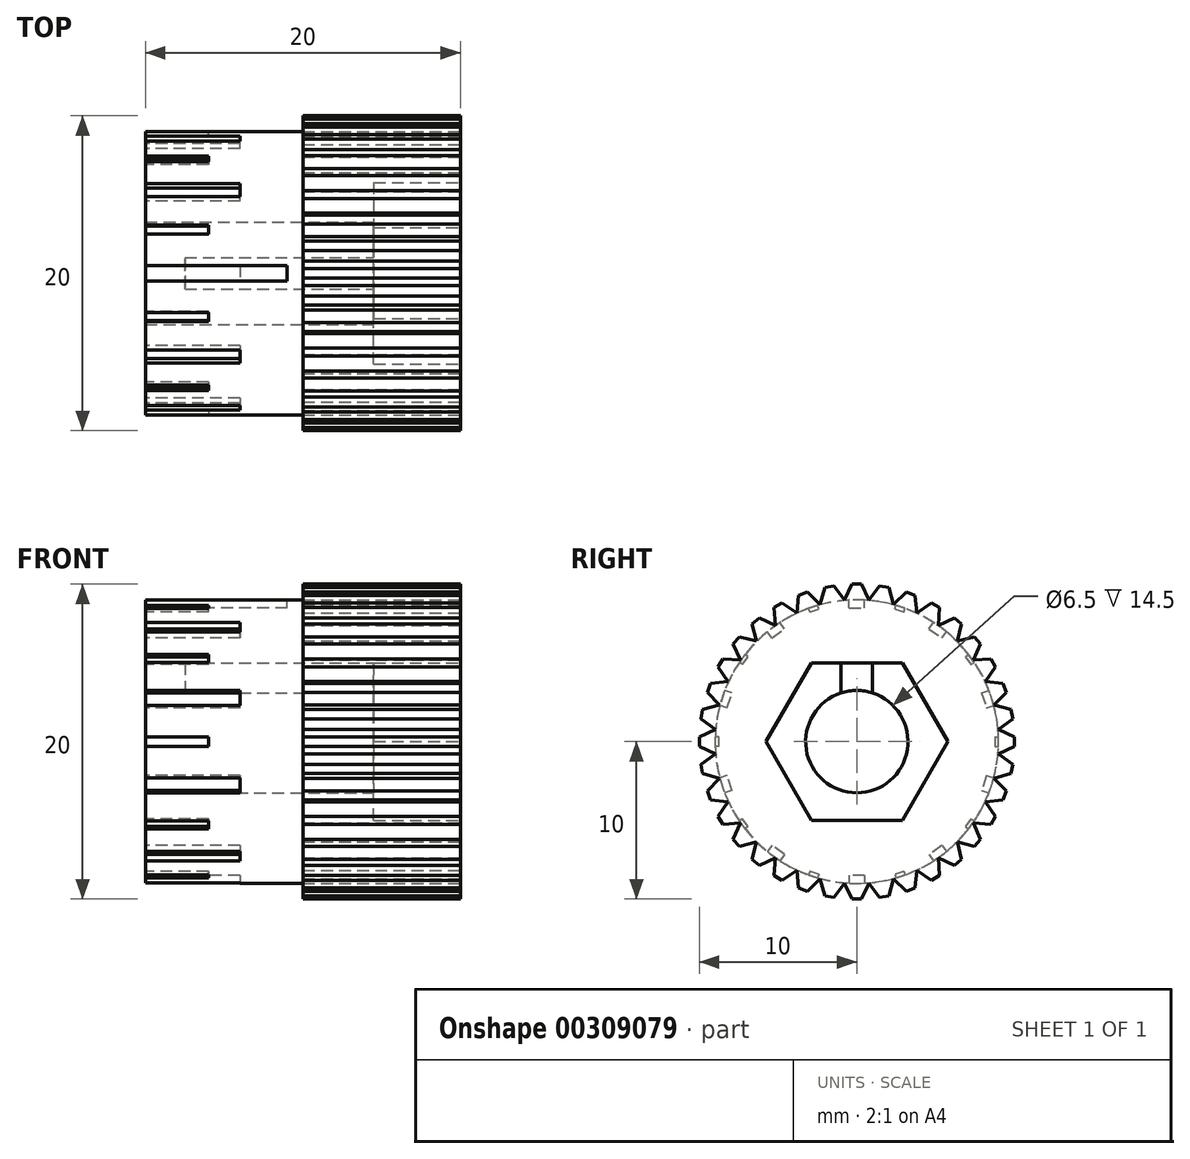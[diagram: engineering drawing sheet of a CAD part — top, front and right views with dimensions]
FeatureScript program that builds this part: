
annotation { "Feature Type Name" : "Feature", "Feature Type Description" : "" }
export const myFeature = defineFeature(function(context is Context, id is Id, definition is map)
    precondition{}
    {
        {
            var Q0;
            Q0=qCreatedBy(makeId("Right.planeOp"),FACE);
            var sketch = newSketch(context, id + "F0", { "sketchPlane" : qUnion([Q0])});
            skCircle(sketch, "E0", {"center": v(0, 0) * mm, "radius": 9 * mm});
            skSolve(sketch);
        }
        {
            var Q0;
            Q0 = qSketchRegion(id + "F0", true);
            extrude(context, id + "F1", {"entities" : qUnion([Q0]), "depth" : 20 * mm});
        }
        {
            var Q0;
            Q0=makeQuery(id+"F1.opExtrude","CAP_FACE",FACE,{"disambiguationData":[OSD([sQuery(id+"F0.wireOp",EDGE,"E0")])],"isStart":false});
            var sketch = newSketch(context, id + "F2", { "sketchPlane" : qUnion([Q0])});
            skLineSegment(sketch, "E1", {"start": v(0, 10) * mm, "end": v(0.3, 10) * mm});
            skLineSegment(sketch, "E2", {"start": v(0.3, 10) * mm, "end": v(0.83, 8.9) * mm});
            skLineSegment(sketch, "E3.MirrorCS", {"start": v(-0.3, 10) * mm, "end": v(-0.83, 8.9) * mm});
            skLineSegment(sketch, "E4.MirrorCS", {"start": v(0, 10) * mm, "end": v(-0.3, 10) * mm});
            skLineSegment(sketch, "E5.1.0", {"start": v(-1.44, 9.9) * mm, "end": v(-0.72, 8.9) * mm});
            skLineSegment(sketch, "E5.1.1", {"start": v(-2.03, 9.8) * mm, "end": v(-2.36, 8.61) * mm});
            skLineSegment(sketch, "E5.1.2", {"start": v(-1.74, 9.85) * mm, "end": v(-1.44, 9.9) * mm});
            skLineSegment(sketch, "E5.1.3", {"start": v(-1.74, 9.85) * mm, "end": v(-2.03, 9.8) * mm});
            skLineSegment(sketch, "E5.2.0", {"start": v(-3.14, 9.5) * mm, "end": v(-2.26, 8.64) * mm});
            skLineSegment(sketch, "E5.2.1", {"start": v(-3.7, 9.3) * mm, "end": v(-3.82, 8.07) * mm});
            skLineSegment(sketch, "E5.2.2", {"start": v(-3.42, 9.4) * mm, "end": v(-3.14, 9.5) * mm});
            skLineSegment(sketch, "E5.2.3", {"start": v(-3.42, 9.4) * mm, "end": v(-3.7, 9.3) * mm});
            skLineSegment(sketch, "E5.3.0", {"start": v(-4.74, 8.81) * mm, "end": v(-3.73, 8.12) * mm});
            skLineSegment(sketch, "E5.3.1", {"start": v(-5.26, 8.51) * mm, "end": v(-5.17, 7.28) * mm});
            skLineSegment(sketch, "E5.3.2", {"start": v(-5, 8.66) * mm, "end": v(-4.74, 8.81) * mm});
            skLineSegment(sketch, "E5.3.3", {"start": v(-5, 8.66) * mm, "end": v(-5.26, 8.51) * mm});
            skLineSegment(sketch, "E5.4.0", {"start": v(-6.2, 7.85) * mm, "end": v(-5.08, 7.35) * mm});
            skLineSegment(sketch, "E5.4.1", {"start": v(-6.66, 7.47) * mm, "end": v(-6.35, 6.28) * mm});
            skLineSegment(sketch, "E5.4.2", {"start": v(-6.43, 7.66) * mm, "end": v(-6.2, 7.85) * mm});
            skLineSegment(sketch, "E5.4.3", {"start": v(-6.43, 7.66) * mm, "end": v(-6.66, 7.47) * mm});
            skLineSegment(sketch, "E5.5.0", {"start": v(-7.47, 6.66) * mm, "end": v(-6.28, 6.35) * mm});
            skLineSegment(sketch, "E5.5.1", {"start": v(-7.85, 6.2) * mm, "end": v(-7.35, 5.08) * mm});
            skLineSegment(sketch, "E5.5.2", {"start": v(-7.66, 6.43) * mm, "end": v(-7.47, 6.66) * mm});
            skLineSegment(sketch, "E5.5.3", {"start": v(-7.66, 6.43) * mm, "end": v(-7.85, 6.2) * mm});
            skLineSegment(sketch, "E5.6.0", {"start": v(-8.51, 5.26) * mm, "end": v(-7.28, 5.17) * mm});
            skLineSegment(sketch, "E5.6.1", {"start": v(-8.81, 4.74) * mm, "end": v(-8.12, 3.73) * mm});
            skLineSegment(sketch, "E5.6.2", {"start": v(-8.66, 5) * mm, "end": v(-8.51, 5.26) * mm});
            skLineSegment(sketch, "E5.6.3", {"start": v(-8.66, 5) * mm, "end": v(-8.81, 4.74) * mm});
            skLineSegment(sketch, "E5.7.0", {"start": v(-9.3, 3.7) * mm, "end": v(-8.07, 3.82) * mm});
            skLineSegment(sketch, "E5.7.1", {"start": v(-9.5, 3.14) * mm, "end": v(-8.64, 2.26) * mm});
            skLineSegment(sketch, "E5.7.2", {"start": v(-9.4, 3.42) * mm, "end": v(-9.3, 3.7) * mm});
            skLineSegment(sketch, "E5.7.3", {"start": v(-9.4, 3.42) * mm, "end": v(-9.5, 3.14) * mm});
            skLineSegment(sketch, "E5.8.0", {"start": v(-9.8, 2.03) * mm, "end": v(-8.61, 2.36) * mm});
            skLineSegment(sketch, "E5.8.1", {"start": v(-9.9, 1.44) * mm, "end": v(-8.9, 0.72) * mm});
            skLineSegment(sketch, "E5.8.2", {"start": v(-9.85, 1.74) * mm, "end": v(-9.8, 2.03) * mm});
            skLineSegment(sketch, "E5.8.3", {"start": v(-9.85, 1.74) * mm, "end": v(-9.9, 1.44) * mm});
            skLineSegment(sketch, "E5.9.0", {"start": v(-10, 0.3) * mm, "end": v(-8.9, 0.83) * mm});
            skLineSegment(sketch, "E5.9.1", {"start": v(-10, -0.3) * mm, "end": v(-8.9, -0.83) * mm});
            skLineSegment(sketch, "E5.9.2", {"start": v(-10, 0) * mm, "end": v(-10, 0.3) * mm});
            skLineSegment(sketch, "E5.9.3", {"start": v(-10, 0) * mm, "end": v(-10, -0.3) * mm});
            skLineSegment(sketch, "E5.10.0", {"start": v(-9.9, -1.44) * mm, "end": v(-8.9, -0.72) * mm});
            skLineSegment(sketch, "E5.10.1", {"start": v(-9.8, -2.03) * mm, "end": v(-8.61, -2.36) * mm});
            skLineSegment(sketch, "E5.10.2", {"start": v(-9.85, -1.74) * mm, "end": v(-9.9, -1.44) * mm});
            skLineSegment(sketch, "E5.10.3", {"start": v(-9.85, -1.74) * mm, "end": v(-9.8, -2.03) * mm});
            skLineSegment(sketch, "E5.11.0", {"start": v(-9.5, -3.14) * mm, "end": v(-8.64, -2.26) * mm});
            skLineSegment(sketch, "E5.11.1", {"start": v(-9.3, -3.7) * mm, "end": v(-8.07, -3.82) * mm});
            skLineSegment(sketch, "E5.11.2", {"start": v(-9.4, -3.42) * mm, "end": v(-9.5, -3.14) * mm});
            skLineSegment(sketch, "E5.11.3", {"start": v(-9.4, -3.42) * mm, "end": v(-9.3, -3.7) * mm});
            skLineSegment(sketch, "E5.12.0", {"start": v(-8.81, -4.74) * mm, "end": v(-8.12, -3.73) * mm});
            skLineSegment(sketch, "E5.12.1", {"start": v(-8.51, -5.26) * mm, "end": v(-7.28, -5.17) * mm});
            skLineSegment(sketch, "E5.12.2", {"start": v(-8.66, -5) * mm, "end": v(-8.81, -4.74) * mm});
            skLineSegment(sketch, "E5.12.3", {"start": v(-8.66, -5) * mm, "end": v(-8.51, -5.26) * mm});
            skLineSegment(sketch, "E5.13.0", {"start": v(-7.85, -6.2) * mm, "end": v(-7.35, -5.08) * mm});
            skLineSegment(sketch, "E5.13.1", {"start": v(-7.47, -6.66) * mm, "end": v(-6.28, -6.35) * mm});
            skLineSegment(sketch, "E5.13.2", {"start": v(-7.66, -6.43) * mm, "end": v(-7.85, -6.2) * mm});
            skLineSegment(sketch, "E5.13.3", {"start": v(-7.66, -6.43) * mm, "end": v(-7.47, -6.66) * mm});
            skLineSegment(sketch, "E5.14.0", {"start": v(-6.66, -7.47) * mm, "end": v(-6.35, -6.28) * mm});
            skLineSegment(sketch, "E5.14.1", {"start": v(-6.2, -7.85) * mm, "end": v(-5.08, -7.35) * mm});
            skLineSegment(sketch, "E5.14.2", {"start": v(-6.43, -7.66) * mm, "end": v(-6.66, -7.47) * mm});
            skLineSegment(sketch, "E5.14.3", {"start": v(-6.43, -7.66) * mm, "end": v(-6.2, -7.85) * mm});
            skLineSegment(sketch, "E5.15.0", {"start": v(-5.26, -8.51) * mm, "end": v(-5.17, -7.28) * mm});
            skLineSegment(sketch, "E5.15.1", {"start": v(-4.74, -8.81) * mm, "end": v(-3.73, -8.12) * mm});
            skLineSegment(sketch, "E5.15.2", {"start": v(-5, -8.66) * mm, "end": v(-5.26, -8.51) * mm});
            skLineSegment(sketch, "E5.15.3", {"start": v(-5, -8.66) * mm, "end": v(-4.74, -8.81) * mm});
            skLineSegment(sketch, "E5.16.0", {"start": v(-3.7, -9.3) * mm, "end": v(-3.82, -8.07) * mm});
            skLineSegment(sketch, "E5.16.1", {"start": v(-3.14, -9.5) * mm, "end": v(-2.26, -8.64) * mm});
            skLineSegment(sketch, "E5.16.2", {"start": v(-3.42, -9.4) * mm, "end": v(-3.7, -9.3) * mm});
            skLineSegment(sketch, "E5.16.3", {"start": v(-3.42, -9.4) * mm, "end": v(-3.14, -9.5) * mm});
            skLineSegment(sketch, "E5.17.0", {"start": v(-2.03, -9.8) * mm, "end": v(-2.36, -8.61) * mm});
            skLineSegment(sketch, "E5.17.1", {"start": v(-1.44, -9.9) * mm, "end": v(-0.72, -8.9) * mm});
            skLineSegment(sketch, "E5.17.2", {"start": v(-1.74, -9.85) * mm, "end": v(-2.03, -9.8) * mm});
            skLineSegment(sketch, "E5.17.3", {"start": v(-1.74, -9.85) * mm, "end": v(-1.44, -9.9) * mm});
            skLineSegment(sketch, "E5.18.0", {"start": v(-0.3, -10) * mm, "end": v(-0.83, -8.9) * mm});
            skLineSegment(sketch, "E5.18.1", {"start": v(0.3, -10) * mm, "end": v(0.83, -8.9) * mm});
            skLineSegment(sketch, "E5.18.2", {"start": v(0, -10) * mm, "end": v(-0.3, -10) * mm});
            skLineSegment(sketch, "E5.18.3", {"start": v(0, -10) * mm, "end": v(0.3, -10) * mm});
            skLineSegment(sketch, "E5.19.0", {"start": v(1.44, -9.9) * mm, "end": v(0.72, -8.9) * mm});
            skLineSegment(sketch, "E5.19.1", {"start": v(2.03, -9.8) * mm, "end": v(2.36, -8.61) * mm});
            skLineSegment(sketch, "E5.19.2", {"start": v(1.74, -9.85) * mm, "end": v(1.44, -9.9) * mm});
            skLineSegment(sketch, "E5.19.3", {"start": v(1.74, -9.85) * mm, "end": v(2.03, -9.8) * mm});
            skLineSegment(sketch, "E5.20.0", {"start": v(3.14, -9.5) * mm, "end": v(2.26, -8.64) * mm});
            skLineSegment(sketch, "E5.20.1", {"start": v(3.7, -9.3) * mm, "end": v(3.82, -8.07) * mm});
            skLineSegment(sketch, "E5.20.2", {"start": v(3.42, -9.4) * mm, "end": v(3.14, -9.5) * mm});
            skLineSegment(sketch, "E5.20.3", {"start": v(3.42, -9.4) * mm, "end": v(3.7, -9.3) * mm});
            skLineSegment(sketch, "E5.21.0", {"start": v(4.74, -8.81) * mm, "end": v(3.73, -8.12) * mm});
            skLineSegment(sketch, "E5.21.1", {"start": v(5.26, -8.51) * mm, "end": v(5.17, -7.28) * mm});
            skLineSegment(sketch, "E5.21.2", {"start": v(5, -8.66) * mm, "end": v(4.74, -8.81) * mm});
            skLineSegment(sketch, "E5.21.3", {"start": v(5, -8.66) * mm, "end": v(5.26, -8.51) * mm});
            skLineSegment(sketch, "E5.22.0", {"start": v(6.2, -7.85) * mm, "end": v(5.08, -7.35) * mm});
            skLineSegment(sketch, "E5.22.1", {"start": v(6.66, -7.47) * mm, "end": v(6.35, -6.28) * mm});
            skLineSegment(sketch, "E5.22.2", {"start": v(6.43, -7.66) * mm, "end": v(6.2, -7.85) * mm});
            skLineSegment(sketch, "E5.22.3", {"start": v(6.43, -7.66) * mm, "end": v(6.66, -7.47) * mm});
            skLineSegment(sketch, "E5.23.0", {"start": v(7.47, -6.66) * mm, "end": v(6.28, -6.35) * mm});
            skLineSegment(sketch, "E5.23.1", {"start": v(7.85, -6.2) * mm, "end": v(7.35, -5.08) * mm});
            skLineSegment(sketch, "E5.23.2", {"start": v(7.66, -6.43) * mm, "end": v(7.47, -6.66) * mm});
            skLineSegment(sketch, "E5.23.3", {"start": v(7.66, -6.43) * mm, "end": v(7.85, -6.2) * mm});
            skLineSegment(sketch, "E5.24.0", {"start": v(8.51, -5.26) * mm, "end": v(7.28, -5.17) * mm});
            skLineSegment(sketch, "E5.24.1", {"start": v(8.81, -4.74) * mm, "end": v(8.12, -3.73) * mm});
            skLineSegment(sketch, "E5.24.2", {"start": v(8.66, -5) * mm, "end": v(8.51, -5.26) * mm});
            skLineSegment(sketch, "E5.24.3", {"start": v(8.66, -5) * mm, "end": v(8.81, -4.74) * mm});
            skLineSegment(sketch, "E5.25.0", {"start": v(9.3, -3.7) * mm, "end": v(8.07, -3.82) * mm});
            skLineSegment(sketch, "E5.25.1", {"start": v(9.5, -3.14) * mm, "end": v(8.64, -2.26) * mm});
            skLineSegment(sketch, "E5.25.2", {"start": v(9.4, -3.42) * mm, "end": v(9.3, -3.7) * mm});
            skLineSegment(sketch, "E5.25.3", {"start": v(9.4, -3.42) * mm, "end": v(9.5, -3.14) * mm});
            skLineSegment(sketch, "E5.26.0", {"start": v(9.8, -2.03) * mm, "end": v(8.61, -2.36) * mm});
            skLineSegment(sketch, "E5.26.1", {"start": v(9.9, -1.44) * mm, "end": v(8.9, -0.72) * mm});
            skLineSegment(sketch, "E5.26.2", {"start": v(9.85, -1.74) * mm, "end": v(9.8, -2.03) * mm});
            skLineSegment(sketch, "E5.26.3", {"start": v(9.85, -1.74) * mm, "end": v(9.9, -1.44) * mm});
            skLineSegment(sketch, "E5.27.0", {"start": v(10, -0.3) * mm, "end": v(8.9, -0.83) * mm});
            skLineSegment(sketch, "E5.27.1", {"start": v(10, 0.3) * mm, "end": v(8.9, 0.83) * mm});
            skLineSegment(sketch, "E5.27.2", {"start": v(10, 0) * mm, "end": v(10, -0.3) * mm});
            skLineSegment(sketch, "E5.27.3", {"start": v(10, 0) * mm, "end": v(10, 0.3) * mm});
            skLineSegment(sketch, "E5.28.0", {"start": v(9.9, 1.44) * mm, "end": v(8.9, 0.72) * mm});
            skLineSegment(sketch, "E5.28.1", {"start": v(9.8, 2.03) * mm, "end": v(8.61, 2.36) * mm});
            skLineSegment(sketch, "E5.28.2", {"start": v(9.85, 1.74) * mm, "end": v(9.9, 1.44) * mm});
            skLineSegment(sketch, "E5.28.3", {"start": v(9.85, 1.74) * mm, "end": v(9.8, 2.03) * mm});
            skLineSegment(sketch, "E5.29.0", {"start": v(9.5, 3.14) * mm, "end": v(8.64, 2.26) * mm});
            skLineSegment(sketch, "E5.29.1", {"start": v(9.3, 3.7) * mm, "end": v(8.07, 3.82) * mm});
            skLineSegment(sketch, "E5.29.2", {"start": v(9.4, 3.42) * mm, "end": v(9.5, 3.14) * mm});
            skLineSegment(sketch, "E5.29.3", {"start": v(9.4, 3.42) * mm, "end": v(9.3, 3.7) * mm});
            skLineSegment(sketch, "E5.30.0", {"start": v(8.81, 4.74) * mm, "end": v(8.12, 3.73) * mm});
            skLineSegment(sketch, "E5.30.1", {"start": v(8.51, 5.26) * mm, "end": v(7.28, 5.17) * mm});
            skLineSegment(sketch, "E5.30.2", {"start": v(8.66, 5) * mm, "end": v(8.81, 4.74) * mm});
            skLineSegment(sketch, "E5.30.3", {"start": v(8.66, 5) * mm, "end": v(8.51, 5.26) * mm});
            skLineSegment(sketch, "E5.31.0", {"start": v(7.85, 6.2) * mm, "end": v(7.35, 5.08) * mm});
            skLineSegment(sketch, "E5.31.1", {"start": v(7.47, 6.66) * mm, "end": v(6.28, 6.35) * mm});
            skLineSegment(sketch, "E5.31.2", {"start": v(7.66, 6.43) * mm, "end": v(7.85, 6.2) * mm});
            skLineSegment(sketch, "E5.31.3", {"start": v(7.66, 6.43) * mm, "end": v(7.47, 6.66) * mm});
            skLineSegment(sketch, "E5.32.0", {"start": v(6.66, 7.47) * mm, "end": v(6.35, 6.28) * mm});
            skLineSegment(sketch, "E5.32.1", {"start": v(6.2, 7.85) * mm, "end": v(5.08, 7.35) * mm});
            skLineSegment(sketch, "E5.32.2", {"start": v(6.43, 7.66) * mm, "end": v(6.66, 7.47) * mm});
            skLineSegment(sketch, "E5.32.3", {"start": v(6.43, 7.66) * mm, "end": v(6.2, 7.85) * mm});
            skLineSegment(sketch, "E5.33.0", {"start": v(5.26, 8.51) * mm, "end": v(5.17, 7.28) * mm});
            skLineSegment(sketch, "E5.33.1", {"start": v(4.74, 8.81) * mm, "end": v(3.73, 8.12) * mm});
            skLineSegment(sketch, "E5.33.2", {"start": v(5, 8.66) * mm, "end": v(5.26, 8.51) * mm});
            skLineSegment(sketch, "E5.33.3", {"start": v(5, 8.66) * mm, "end": v(4.74, 8.81) * mm});
            skLineSegment(sketch, "E5.34.0", {"start": v(3.7, 9.3) * mm, "end": v(3.82, 8.07) * mm});
            skLineSegment(sketch, "E5.34.1", {"start": v(3.14, 9.5) * mm, "end": v(2.26, 8.64) * mm});
            skLineSegment(sketch, "E5.34.2", {"start": v(3.42, 9.4) * mm, "end": v(3.7, 9.3) * mm});
            skLineSegment(sketch, "E5.34.3", {"start": v(3.42, 9.4) * mm, "end": v(3.14, 9.5) * mm});
            skLineSegment(sketch, "E5.35.0", {"start": v(2.03, 9.8) * mm, "end": v(2.36, 8.61) * mm});
            skLineSegment(sketch, "E5.35.1", {"start": v(1.44, 9.9) * mm, "end": v(0.72, 8.9) * mm});
            skLineSegment(sketch, "E5.35.2", {"start": v(1.74, 9.85) * mm, "end": v(2.03, 9.8) * mm});
            skLineSegment(sketch, "E5.35.3", {"start": v(1.74, 9.85) * mm, "end": v(1.44, 9.9) * mm});
            skPoint(sketch, "E5.center", {"position": v(0, 0) * mm});
            skCircle(sketch, "E6.0", {"center": v(0, 0) * mm, "radius": 9 * mm});
            skArc(sketch, "E7.0.0", {"start": v(-3.82, 8.15) * mm, "mid": v(2.33, -8.7) * mm, "end": v(-0.77, 8.97) * mm});
            skArc(sketch, "E8.trimOffspring", {"start": v(-2.34, 8.69) * mm, "mid": v(2.33, -8.7) * mm, "end": v(-2.32, 8.7) * mm});
            skSolve(sketch);
        }
        {
            var Q0;
            Q0 = qSketchRegion(id + "F2", true);
            extrude(context, id + "F3", {"entities" : qUnion([Q0]), "operationType" : NewBodyOperationType.ADD, "oppositeDirection" : true, "depth" : 10 * mm});
        }
        {
            var Q0;
            Q0=makeQuery(id+"F1.opExtrude","CAP_FACE",FACE,{"disambiguationData":[OSD([sQuery(id+"F0.wireOp",EDGE,"E0")])],"isStart":false});
            var sketch = newSketch(context, id + "F4", { "sketchPlane" : qUnion([Q0])});
            skCircle(sketch, "E9", {"center": v(0, 0) * mm, "radius": 3.25 * mm});
            skSolve(sketch);
        }
        {
            var Q0;
            Q0=makeQuery(id+"F1.opExtrude","CAP_FACE",FACE,{"disambiguationData":[OSD([sQuery(id+"F0.wireOp",EDGE,"E0")])],"isStart":false});
            var sketch = newSketch(context, id + "F5", { "sketchPlane" : qUnion([Q0])});
            skCircle(sketch, "E10.cCircle", {"center": v(0, 0) * mm, "radius": 5 * mm, "construction": true});
            skLineSegment(sketch, "E10.0", {"start": v(5.77, 0) * mm, "end": v(2.89, -5) * mm});
            skLineSegment(sketch, "E10.1", {"start": v(2.89, -5) * mm, "end": v(-2.89, -5) * mm});
            skLineSegment(sketch, "E10.2", {"start": v(-2.89, -5) * mm, "end": v(-5.77, 0) * mm});
            skLineSegment(sketch, "E10.3", {"start": v(-5.77, 0) * mm, "end": v(-2.89, 5) * mm});
            skLineSegment(sketch, "E10.4", {"start": v(-2.89, 5) * mm, "end": v(2.89, 5) * mm});
            skLineSegment(sketch, "E10.5", {"start": v(2.89, 5) * mm, "end": v(5.77, 0) * mm});
            skPoint(sketch, "E10.0.midPoint", {"position": v(4.33, -2.5) * mm});
            skSolve(sketch);
        }
        {
            var Q0;
            Q0 = qSketchRegion(id + "F5", true);
            extrude(context, id + "F6", {"entities" : qUnion([Q0]), "operationType" : NewBodyOperationType.REMOVE, "oppositeDirection" : true, "depth" : 5.5 * mm});
        }
        {
            var Q0;
            Q0=makeQuery(id+"F6.boolean.opBoolean","COPY",FACE,{"derivedFrom":makeQuery(id+"F6.opExtrude","CAP_FACE",FACE,{"disambiguationData":[OSD([sQuery(id+"F5.wireOp",EDGE,"E10.0"),sQuery(id+"F5.wireOp",EDGE,"E10.1"),sQuery(id+"F5.wireOp",EDGE,"E10.2"),sQuery(id+"F5.wireOp",EDGE,"E10.3"),sQuery(id+"F5.wireOp",EDGE,"E10.4"),sQuery(id+"F5.wireOp",EDGE,"E10.5")])],"isStart":false})});
            var sketch = newSketch(context, id + "F7", { "sketchPlane" : qUnion([Q0])});
            skLineSegment(sketch, "E11.bottom", {"start": v(1, 5) * mm, "end": v(-1, 5) * mm});
            skLineSegment(sketch, "E11.top", {"start": v(1, 3) * mm, "end": v(-1, 3) * mm});
            skLineSegment(sketch, "E11.left", {"start": v(1, 5) * mm, "end": v(1, 3) * mm});
            skLineSegment(sketch, "E11.right", {"start": v(-1, 5) * mm, "end": v(-1, 3) * mm});
            skPoint(sketch, "E11.middle", {"position": v(0, 4) * mm});
            skSolve(sketch);
        }
        {
            var Q0;
            Q0 = qSketchRegion(id + "F7", true);
            extrude(context, id + "F8", {"entities" : qUnion([Q0]), "operationType" : NewBodyOperationType.REMOVE, "oppositeDirection" : true, "depth" : 12 * mm});
        }
        {
            var Q0;
            Q0=makeQuery(id+"F1.opExtrude","CAP_FACE",FACE,{"disambiguationData":[OSD([sQuery(id+"F0.wireOp",EDGE,"E0")])],"isStart":true});
            var sketch = newSketch(context, id + "F9", { "sketchPlane" : qUnion([Q0])});
            skLineSegment(sketch, "E12.bottom", {"start": v(0.5, 8.5) * mm, "end": v(-0.5, 8.5) * mm});
            skLineSegment(sketch, "E12.top", {"start": v(0.5, 9.5) * mm, "end": v(-0.5, 9.5) * mm});
            skLineSegment(sketch, "E12.left", {"start": v(0.5, 8.5) * mm, "end": v(0.5, 9.5) * mm});
            skLineSegment(sketch, "E12.right", {"start": v(-0.5, 8.5) * mm, "end": v(-0.5, 9.5) * mm});
            skPoint(sketch, "E12.middle", {"position": v(0, 9) * mm});
            skLineSegment(sketch, "E13.1.0", {"start": v(-5.4, 6.58) * mm, "end": v(-5.99, 7.4) * mm});
            skLineSegment(sketch, "E13.1.1", {"start": v(-4.6, 7.17) * mm, "end": v(-5.18, 7.98) * mm});
            skLineSegment(sketch, "E13.1.2", {"start": v(-5.18, 7.98) * mm, "end": v(-5.99, 7.4) * mm});
            skLineSegment(sketch, "E13.1.3", {"start": v(-4.6, 7.17) * mm, "end": v(-5.4, 6.58) * mm});
            skPoint(sketch, "E13.1.4", {"position": v(-5.3, 7.28) * mm});
            skLineSegment(sketch, "E13.2.0", {"start": v(-8.24, 2.15) * mm, "end": v(-9.19, 2.46) * mm});
            skLineSegment(sketch, "E13.2.1", {"start": v(-7.93, 3.1) * mm, "end": v(-8.88, 3.41) * mm});
            skLineSegment(sketch, "E13.2.2", {"start": v(-8.88, 3.41) * mm, "end": v(-9.19, 2.46) * mm});
            skLineSegment(sketch, "E13.2.3", {"start": v(-7.93, 3.1) * mm, "end": v(-8.24, 2.15) * mm});
            skPoint(sketch, "E13.2.4", {"position": v(-8.56, 2.78) * mm});
            skLineSegment(sketch, "E13.3.0", {"start": v(-7.93, -3.1) * mm, "end": v(-8.88, -3.41) * mm});
            skLineSegment(sketch, "E13.3.1", {"start": v(-8.24, -2.15) * mm, "end": v(-9.19, -2.46) * mm});
            skLineSegment(sketch, "E13.3.2", {"start": v(-9.19, -2.46) * mm, "end": v(-8.88, -3.41) * mm});
            skLineSegment(sketch, "E13.3.3", {"start": v(-8.24, -2.15) * mm, "end": v(-7.93, -3.1) * mm});
            skPoint(sketch, "E13.3.4", {"position": v(-8.56, -2.78) * mm});
            skLineSegment(sketch, "E13.4.0", {"start": v(-4.6, -7.17) * mm, "end": v(-5.18, -7.98) * mm});
            skLineSegment(sketch, "E13.4.1", {"start": v(-5.4, -6.58) * mm, "end": v(-5.99, -7.4) * mm});
            skLineSegment(sketch, "E13.4.2", {"start": v(-5.99, -7.4) * mm, "end": v(-5.18, -7.98) * mm});
            skLineSegment(sketch, "E13.4.3", {"start": v(-5.4, -6.58) * mm, "end": v(-4.6, -7.17) * mm});
            skPoint(sketch, "E13.4.4", {"position": v(-5.3, -7.28) * mm});
            skLineSegment(sketch, "E13.5.0", {"start": v(0.5, -8.5) * mm, "end": v(0.5, -9.5) * mm});
            skLineSegment(sketch, "E13.5.1", {"start": v(-0.5, -8.5) * mm, "end": v(-0.5, -9.5) * mm});
            skLineSegment(sketch, "E13.5.2", {"start": v(-0.5, -9.5) * mm, "end": v(0.5, -9.5) * mm});
            skLineSegment(sketch, "E13.5.3", {"start": v(-0.5, -8.5) * mm, "end": v(0.5, -8.5) * mm});
            skPoint(sketch, "E13.5.4", {"position": v(0, -9) * mm});
            skLineSegment(sketch, "E13.6.0", {"start": v(5.4, -6.58) * mm, "end": v(5.99, -7.4) * mm});
            skLineSegment(sketch, "E13.6.1", {"start": v(4.6, -7.17) * mm, "end": v(5.18, -7.98) * mm});
            skLineSegment(sketch, "E13.6.2", {"start": v(5.18, -7.98) * mm, "end": v(5.99, -7.4) * mm});
            skLineSegment(sketch, "E13.6.3", {"start": v(4.6, -7.17) * mm, "end": v(5.4, -6.58) * mm});
            skPoint(sketch, "E13.6.4", {"position": v(5.3, -7.28) * mm});
            skLineSegment(sketch, "E13.7.0", {"start": v(8.24, -2.15) * mm, "end": v(9.19, -2.46) * mm});
            skLineSegment(sketch, "E13.7.1", {"start": v(7.93, -3.1) * mm, "end": v(8.88, -3.41) * mm});
            skLineSegment(sketch, "E13.7.2", {"start": v(8.88, -3.41) * mm, "end": v(9.19, -2.46) * mm});
            skLineSegment(sketch, "E13.7.3", {"start": v(7.93, -3.1) * mm, "end": v(8.24, -2.15) * mm});
            skPoint(sketch, "E13.7.4", {"position": v(8.56, -2.78) * mm});
            skLineSegment(sketch, "E13.8.0", {"start": v(7.93, 3.1) * mm, "end": v(8.88, 3.41) * mm});
            skLineSegment(sketch, "E13.8.1", {"start": v(8.24, 2.15) * mm, "end": v(9.19, 2.46) * mm});
            skLineSegment(sketch, "E13.8.2", {"start": v(9.19, 2.46) * mm, "end": v(8.88, 3.41) * mm});
            skLineSegment(sketch, "E13.8.3", {"start": v(8.24, 2.15) * mm, "end": v(7.93, 3.1) * mm});
            skPoint(sketch, "E13.8.4", {"position": v(8.56, 2.78) * mm});
            skLineSegment(sketch, "E13.9.0", {"start": v(4.6, 7.17) * mm, "end": v(5.18, 7.98) * mm});
            skLineSegment(sketch, "E13.9.1", {"start": v(5.4, 6.58) * mm, "end": v(5.99, 7.4) * mm});
            skLineSegment(sketch, "E13.9.2", {"start": v(5.99, 7.4) * mm, "end": v(5.18, 7.98) * mm});
            skLineSegment(sketch, "E13.9.3", {"start": v(5.4, 6.58) * mm, "end": v(4.6, 7.17) * mm});
            skPoint(sketch, "E13.9.4", {"position": v(5.3, 7.28) * mm});
            skPoint(sketch, "E13.center", {"position": v(0, 0) * mm});
            skSolve(sketch);
        }
        {
            var Q0;
            Q0 = qSketchRegion(id + "F9", true);
            extrude(context, id + "F10", {"entities" : qUnion([Q0]), "operationType" : NewBodyOperationType.REMOVE, "oppositeDirection" : true, "depth" : 6 * mm});
        }
        {
            var Q0;
            Q0=makeQuery(id+"F1.opExtrude","CAP_FACE",FACE,{"disambiguationData":[OSD([sQuery(id+"F0.wireOp",EDGE,"E0")])],"isStart":true});
            var sketch = newSketch(context, id + "F11", { "sketchPlane" : qUnion([Q0])});
            skLineSegment(sketch, "E14.bottom", {"start": v(-0.3, -8.75) * mm, "end": v(0.3, -8.75) * mm});
            skLineSegment(sketch, "E14.top", {"start": v(-0.3, -9.25) * mm, "end": v(0.3, -9.25) * mm});
            skLineSegment(sketch, "E14.left", {"start": v(-0.3, -8.75) * mm, "end": v(-0.3, -9.25) * mm});
            skLineSegment(sketch, "E14.right", {"start": v(0.3, -8.75) * mm, "end": v(0.3, -9.25) * mm});
            skPoint(sketch, "E14.middle", {"position": v(0, -9) * mm});
            skLineSegment(sketch, "E15.1.0", {"start": v(2.42, -8.42) * mm, "end": v(3, -8.23) * mm});
            skLineSegment(sketch, "E15.1.1", {"start": v(2.42, -8.42) * mm, "end": v(2.57, -8.9) * mm});
            skLineSegment(sketch, "E15.1.2", {"start": v(3, -8.23) * mm, "end": v(3.15, -8.7) * mm});
            skPoint(sketch, "E15.1.3", {"position": v(2.78, -8.56) * mm});
            skLineSegment(sketch, "E15.1.4", {"start": v(2.57, -8.9) * mm, "end": v(3.15, -8.7) * mm});
            skLineSegment(sketch, "E15.2.0", {"start": v(4.9, -7.26) * mm, "end": v(5.39, -6.9) * mm});
            skLineSegment(sketch, "E15.2.1", {"start": v(4.9, -7.26) * mm, "end": v(5.2, -7.66) * mm});
            skLineSegment(sketch, "E15.2.2", {"start": v(5.39, -6.9) * mm, "end": v(5.68, -7.31) * mm});
            skPoint(sketch, "E15.2.3", {"position": v(5.3, -7.28) * mm});
            skLineSegment(sketch, "E15.2.4", {"start": v(5.2, -7.66) * mm, "end": v(5.68, -7.31) * mm});
            skLineSegment(sketch, "E15.3.0", {"start": v(6.9, -5.39) * mm, "end": v(7.26, -4.9) * mm});
            skLineSegment(sketch, "E15.3.1", {"start": v(6.9, -5.39) * mm, "end": v(7.31, -5.68) * mm});
            skLineSegment(sketch, "E15.3.2", {"start": v(7.26, -4.9) * mm, "end": v(7.66, -5.2) * mm});
            skPoint(sketch, "E15.3.3", {"position": v(7.28, -5.3) * mm});
            skLineSegment(sketch, "E15.3.4", {"start": v(7.31, -5.68) * mm, "end": v(7.66, -5.2) * mm});
            skLineSegment(sketch, "E15.4.0", {"start": v(8.23, -3) * mm, "end": v(8.42, -2.42) * mm});
            skLineSegment(sketch, "E15.4.1", {"start": v(8.23, -3) * mm, "end": v(8.7, -3.15) * mm});
            skLineSegment(sketch, "E15.4.2", {"start": v(8.42, -2.42) * mm, "end": v(8.9, -2.57) * mm});
            skPoint(sketch, "E15.4.3", {"position": v(8.56, -2.78) * mm});
            skLineSegment(sketch, "E15.4.4", {"start": v(8.7, -3.15) * mm, "end": v(8.9, -2.57) * mm});
            skLineSegment(sketch, "E15.5.0", {"start": v(8.75, -0.3) * mm, "end": v(8.75, 0.3) * mm});
            skLineSegment(sketch, "E15.5.1", {"start": v(8.75, -0.3) * mm, "end": v(9.25, -0.3) * mm});
            skLineSegment(sketch, "E15.5.2", {"start": v(8.75, 0.3) * mm, "end": v(9.25, 0.3) * mm});
            skPoint(sketch, "E15.5.3", {"position": v(9, 0) * mm});
            skLineSegment(sketch, "E15.5.4", {"start": v(9.25, -0.3) * mm, "end": v(9.25, 0.3) * mm});
            skLineSegment(sketch, "E15.6.0", {"start": v(8.42, 2.42) * mm, "end": v(8.23, 3) * mm});
            skLineSegment(sketch, "E15.6.1", {"start": v(8.42, 2.42) * mm, "end": v(8.9, 2.57) * mm});
            skLineSegment(sketch, "E15.6.2", {"start": v(8.23, 3) * mm, "end": v(8.7, 3.15) * mm});
            skPoint(sketch, "E15.6.3", {"position": v(8.56, 2.78) * mm});
            skLineSegment(sketch, "E15.6.4", {"start": v(8.9, 2.57) * mm, "end": v(8.7, 3.15) * mm});
            skLineSegment(sketch, "E15.7.0", {"start": v(7.26, 4.9) * mm, "end": v(6.9, 5.39) * mm});
            skLineSegment(sketch, "E15.7.1", {"start": v(7.26, 4.9) * mm, "end": v(7.66, 5.2) * mm});
            skLineSegment(sketch, "E15.7.2", {"start": v(6.9, 5.39) * mm, "end": v(7.31, 5.68) * mm});
            skPoint(sketch, "E15.7.3", {"position": v(7.28, 5.3) * mm});
            skLineSegment(sketch, "E15.7.4", {"start": v(7.66, 5.2) * mm, "end": v(7.31, 5.68) * mm});
            skLineSegment(sketch, "E15.8.0", {"start": v(5.39, 6.9) * mm, "end": v(4.9, 7.26) * mm});
            skLineSegment(sketch, "E15.8.1", {"start": v(5.39, 6.9) * mm, "end": v(5.68, 7.31) * mm});
            skLineSegment(sketch, "E15.8.2", {"start": v(4.9, 7.26) * mm, "end": v(5.2, 7.66) * mm});
            skPoint(sketch, "E15.8.3", {"position": v(5.3, 7.28) * mm});
            skLineSegment(sketch, "E15.8.4", {"start": v(5.68, 7.31) * mm, "end": v(5.2, 7.66) * mm});
            skLineSegment(sketch, "E15.9.0", {"start": v(3, 8.23) * mm, "end": v(2.42, 8.42) * mm});
            skLineSegment(sketch, "E15.9.1", {"start": v(3, 8.23) * mm, "end": v(3.15, 8.7) * mm});
            skLineSegment(sketch, "E15.9.2", {"start": v(2.42, 8.42) * mm, "end": v(2.57, 8.9) * mm});
            skPoint(sketch, "E15.9.3", {"position": v(2.78, 8.56) * mm});
            skLineSegment(sketch, "E15.9.4", {"start": v(3.15, 8.7) * mm, "end": v(2.57, 8.9) * mm});
            skLineSegment(sketch, "E15.10.0", {"start": v(0.3, 8.75) * mm, "end": v(-0.3, 8.75) * mm});
            skLineSegment(sketch, "E15.10.1", {"start": v(0.3, 8.75) * mm, "end": v(0.3, 9.25) * mm});
            skLineSegment(sketch, "E15.10.2", {"start": v(-0.3, 8.75) * mm, "end": v(-0.3, 9.25) * mm});
            skPoint(sketch, "E15.10.3", {"position": v(0, 9) * mm});
            skLineSegment(sketch, "E15.10.4", {"start": v(0.3, 9.25) * mm, "end": v(-0.3, 9.25) * mm});
            skLineSegment(sketch, "E15.11.0", {"start": v(-2.42, 8.42) * mm, "end": v(-3, 8.23) * mm});
            skLineSegment(sketch, "E15.11.1", {"start": v(-2.42, 8.42) * mm, "end": v(-2.57, 8.9) * mm});
            skLineSegment(sketch, "E15.11.2", {"start": v(-3, 8.23) * mm, "end": v(-3.15, 8.7) * mm});
            skPoint(sketch, "E15.11.3", {"position": v(-2.78, 8.56) * mm});
            skLineSegment(sketch, "E15.11.4", {"start": v(-2.57, 8.9) * mm, "end": v(-3.15, 8.7) * mm});
            skLineSegment(sketch, "E15.12.0", {"start": v(-4.9, 7.26) * mm, "end": v(-5.39, 6.9) * mm});
            skLineSegment(sketch, "E15.12.1", {"start": v(-4.9, 7.26) * mm, "end": v(-5.2, 7.66) * mm});
            skLineSegment(sketch, "E15.12.2", {"start": v(-5.39, 6.9) * mm, "end": v(-5.68, 7.31) * mm});
            skPoint(sketch, "E15.12.3", {"position": v(-5.3, 7.28) * mm});
            skLineSegment(sketch, "E15.12.4", {"start": v(-5.2, 7.66) * mm, "end": v(-5.68, 7.31) * mm});
            skLineSegment(sketch, "E15.13.0", {"start": v(-6.9, 5.39) * mm, "end": v(-7.26, 4.9) * mm});
            skLineSegment(sketch, "E15.13.1", {"start": v(-6.9, 5.39) * mm, "end": v(-7.31, 5.68) * mm});
            skLineSegment(sketch, "E15.13.2", {"start": v(-7.26, 4.9) * mm, "end": v(-7.66, 5.2) * mm});
            skPoint(sketch, "E15.13.3", {"position": v(-7.28, 5.3) * mm});
            skLineSegment(sketch, "E15.13.4", {"start": v(-7.31, 5.68) * mm, "end": v(-7.66, 5.2) * mm});
            skLineSegment(sketch, "E15.14.0", {"start": v(-8.23, 3) * mm, "end": v(-8.42, 2.42) * mm});
            skLineSegment(sketch, "E15.14.1", {"start": v(-8.23, 3) * mm, "end": v(-8.7, 3.15) * mm});
            skLineSegment(sketch, "E15.14.2", {"start": v(-8.42, 2.42) * mm, "end": v(-8.9, 2.57) * mm});
            skPoint(sketch, "E15.14.3", {"position": v(-8.56, 2.78) * mm});
            skLineSegment(sketch, "E15.14.4", {"start": v(-8.7, 3.15) * mm, "end": v(-8.9, 2.57) * mm});
            skLineSegment(sketch, "E15.15.0", {"start": v(-8.75, 0.3) * mm, "end": v(-8.75, -0.3) * mm});
            skLineSegment(sketch, "E15.15.1", {"start": v(-8.75, 0.3) * mm, "end": v(-9.25, 0.3) * mm});
            skLineSegment(sketch, "E15.15.2", {"start": v(-8.75, -0.3) * mm, "end": v(-9.25, -0.3) * mm});
            skPoint(sketch, "E15.15.3", {"position": v(-9, 0) * mm});
            skLineSegment(sketch, "E15.15.4", {"start": v(-9.25, 0.3) * mm, "end": v(-9.25, -0.3) * mm});
            skLineSegment(sketch, "E15.16.0", {"start": v(-8.42, -2.42) * mm, "end": v(-8.23, -3) * mm});
            skLineSegment(sketch, "E15.16.1", {"start": v(-8.42, -2.42) * mm, "end": v(-8.9, -2.57) * mm});
            skLineSegment(sketch, "E15.16.2", {"start": v(-8.23, -3) * mm, "end": v(-8.7, -3.15) * mm});
            skPoint(sketch, "E15.16.3", {"position": v(-8.56, -2.78) * mm});
            skLineSegment(sketch, "E15.16.4", {"start": v(-8.9, -2.57) * mm, "end": v(-8.7, -3.15) * mm});
            skLineSegment(sketch, "E15.17.0", {"start": v(-7.26, -4.9) * mm, "end": v(-6.9, -5.39) * mm});
            skLineSegment(sketch, "E15.17.1", {"start": v(-7.26, -4.9) * mm, "end": v(-7.66, -5.2) * mm});
            skLineSegment(sketch, "E15.17.2", {"start": v(-6.9, -5.39) * mm, "end": v(-7.31, -5.68) * mm});
            skPoint(sketch, "E15.17.3", {"position": v(-7.28, -5.3) * mm});
            skLineSegment(sketch, "E15.17.4", {"start": v(-7.66, -5.2) * mm, "end": v(-7.31, -5.68) * mm});
            skLineSegment(sketch, "E15.18.0", {"start": v(-5.39, -6.9) * mm, "end": v(-4.9, -7.26) * mm});
            skLineSegment(sketch, "E15.18.1", {"start": v(-5.39, -6.9) * mm, "end": v(-5.68, -7.31) * mm});
            skLineSegment(sketch, "E15.18.2", {"start": v(-4.9, -7.26) * mm, "end": v(-5.2, -7.66) * mm});
            skPoint(sketch, "E15.18.3", {"position": v(-5.3, -7.28) * mm});
            skLineSegment(sketch, "E15.18.4", {"start": v(-5.68, -7.31) * mm, "end": v(-5.2, -7.66) * mm});
            skLineSegment(sketch, "E15.19.0", {"start": v(-3, -8.23) * mm, "end": v(-2.42, -8.42) * mm});
            skLineSegment(sketch, "E15.19.1", {"start": v(-3, -8.23) * mm, "end": v(-3.15, -8.7) * mm});
            skLineSegment(sketch, "E15.19.2", {"start": v(-2.42, -8.42) * mm, "end": v(-2.57, -8.9) * mm});
            skPoint(sketch, "E15.19.3", {"position": v(-2.78, -8.56) * mm});
            skLineSegment(sketch, "E15.19.4", {"start": v(-3.15, -8.7) * mm, "end": v(-2.57, -8.9) * mm});
            skPoint(sketch, "E15.center", {"position": v(0, 0) * mm});
            skSolve(sketch);
        }
        {
            var Q0;
            Q0 = qSketchRegion(id + "F11", true);
            extrude(context, id + "F12", {"entities" : qUnion([Q0]), "operationType" : NewBodyOperationType.REMOVE, "oppositeDirection" : true, "depth" : 4 * mm});
        }
        {
            var Q0;
            Q0=makeQuery(id+"F4.imprint","IMPRINT",FACE,{"disambiguationData":[TD([[makeQuery(id+"F4.imprint","IMPRINT",EDGE,{"derivedFrom":sQuery(id+"F4.wireOp",EDGE,"E9")}),1.0]])]});
            var Q1;
            Q1=sQuery(id+"F4.wireOp",EDGE,"E9");
            extrude(context, id + "F13", {"entities" : qUnion([Q0]), "operationType" : NewBodyOperationType.REMOVE, "surfaceEntities" : qUnion([Q1]), "endBound" : BoundingType.THROUGH_ALL, "oppositeDirection" : true, "depth" : 25 * mm});
        }
        {
            var Q0;
            Q0=makeQuery(id+"F1.opExtrude","CAP_FACE",FACE,{"disambiguationData":[OSD([sQuery(id+"F0.wireOp",EDGE,"E0")])],"isStart":true});
            var sketch = newSketch(context, id + "F14", { "sketchPlane" : qUnion([Q0])});
            skLineSegment(sketch, "E16.bottom", {"start": v(0.5, 8.5) * mm, "end": v(-0.5, 8.5) * mm});
            skLineSegment(sketch, "E16.top", {"start": v(0.5, 9) * mm, "end": v(-0.5, 9) * mm});
            skLineSegment(sketch, "E16.left", {"start": v(0.5, 8.5) * mm, "end": v(0.5, 9) * mm});
            skLineSegment(sketch, "E16.right", {"start": v(-0.5, 8.5) * mm, "end": v(-0.5, 9) * mm});
            skPoint(sketch, "E16.middle", {"position": v(0, 8.75) * mm});
            skPoint(sketch, "E17.center", {"position": v(0, 0) * mm});
            skSolve(sketch);
        }
        {
            var Q0;
            Q0 = qSketchRegion(id + "F14", true);
            extrude(context, id + "F15", {"entities" : qUnion([Q0]), "operationType" : NewBodyOperationType.REMOVE, "oppositeDirection" : true, "depth" : 9 * mm});
        }
    });
